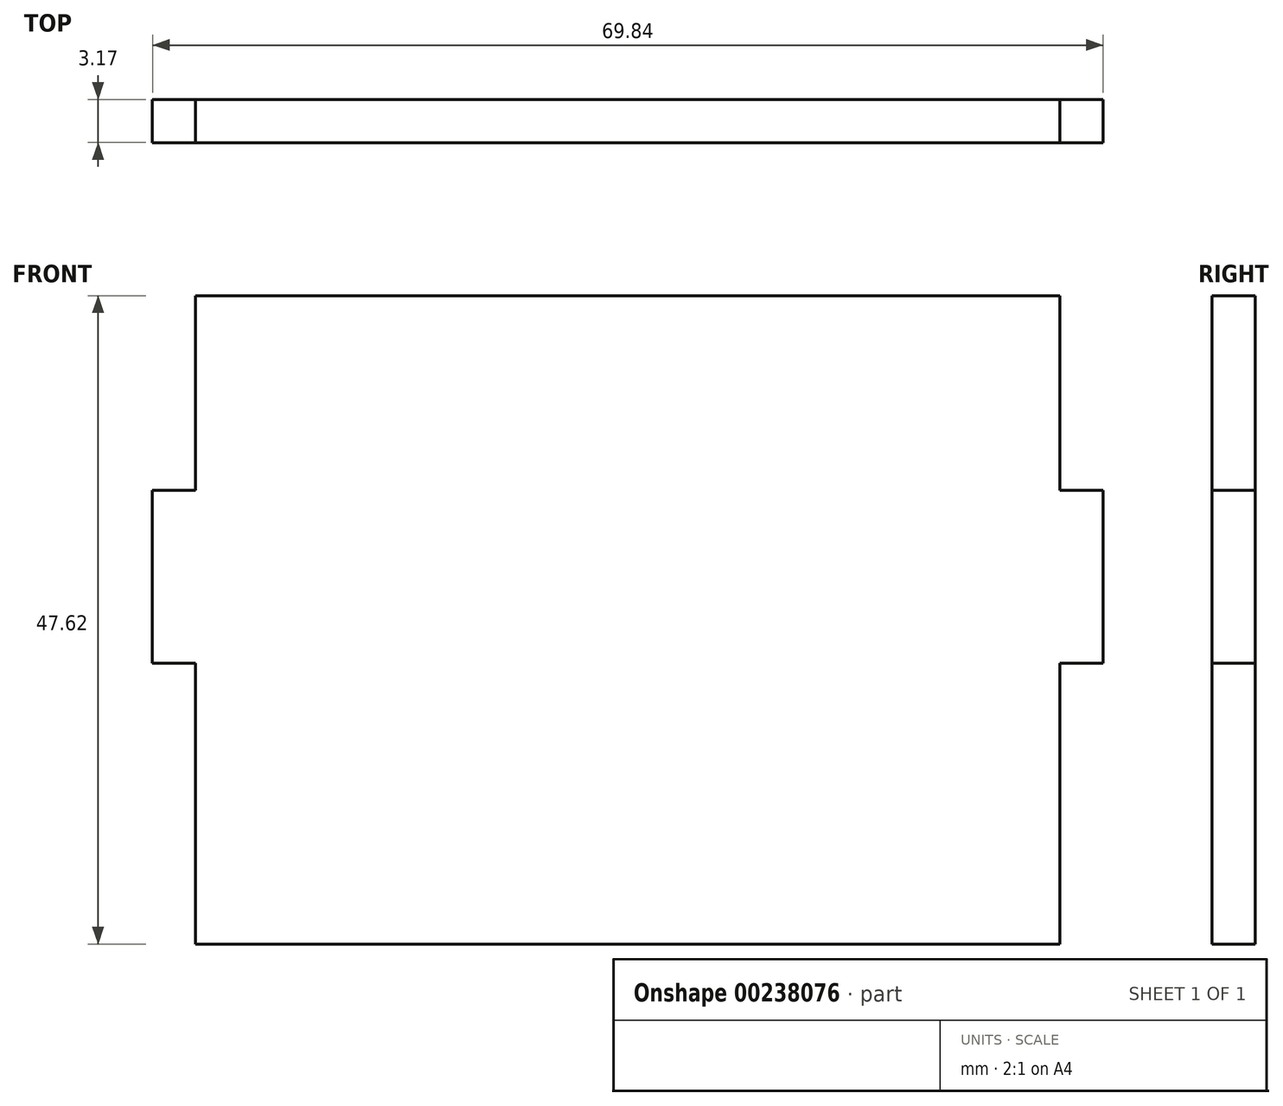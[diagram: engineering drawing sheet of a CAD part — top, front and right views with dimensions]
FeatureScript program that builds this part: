
annotation { "Feature Type Name" : "Feature", "Feature Type Description" : "" }
export const myFeature = defineFeature(function(context is Context, id is Id, definition is map)
    precondition{}
    {
        {
            var Q0;
            Q0=qCreatedBy(makeId("Front.planeOp"),FACE);
            var sketch = newSketch(context, id + "F0", { "sketchPlane" : qUnion([Q0])});
            skLineSegment(sketch, "E0.bottom", {"start": v(31.75, -23.81) * mm, "end": v(-31.75, -23.81) * mm});
            skLineSegment(sketch, "E0.top", {"start": v(31.75, 23.81) * mm, "end": v(-31.75, 23.81) * mm});
            skLineSegment(sketch, "E0.left", {"start": v(31.75, -23.81) * mm, "end": v(31.75, 23.81) * mm});
            skLineSegment(sketch, "E0.right", {"start": v(-31.75, -23.81) * mm, "end": v(-31.75, 23.81) * mm});
            skPoint(sketch, "E0.middle", {"position": v(0, 0) * mm});
            skLineSegment(sketch, "E1.bottom", {"start": v(31.75, 9.52) * mm, "end": v(34.92, 9.52) * mm});
            skLineSegment(sketch, "E1.top", {"start": v(31.75, -3.17) * mm, "end": v(34.92, -3.17) * mm});
            skLineSegment(sketch, "E1.left", {"start": v(31.75, 9.52) * mm, "end": v(31.75, -3.17) * mm});
            skLineSegment(sketch, "E1.right", {"start": v(34.92, 9.52) * mm, "end": v(34.92, -3.17) * mm});
            skLineSegment(sketch, "E2.bottom", {"start": v(-34.92, 9.52) * mm, "end": v(-31.75, 9.52) * mm});
            skLineSegment(sketch, "E2.top", {"start": v(-34.92, -3.17) * mm, "end": v(-31.75, -3.17) * mm});
            skLineSegment(sketch, "E2.left", {"start": v(-34.92, 9.52) * mm, "end": v(-34.92, -3.17) * mm});
            skLineSegment(sketch, "E2.right", {"start": v(-31.75, 9.52) * mm, "end": v(-31.75, -3.17) * mm});
            skLineSegment(sketch, "E3.bottom", {"start": v(-6.35, -23.81) * mm, "end": v(6.35, -23.81) * mm});
            skLineSegment(sketch, "E3.top", {"start": v(-6.35, -26.99) * mm, "end": v(6.35, -26.99) * mm});
            skLineSegment(sketch, "E3.left", {"start": v(-6.35, -23.81) * mm, "end": v(-6.35, -26.99) * mm});
            skLineSegment(sketch, "E3.right", {"start": v(6.35, -23.81) * mm, "end": v(6.35, -26.99) * mm});
            skSolve(sketch);
        }
        {
            var Q0;
            {var subQ4=sQuery(id+"F0.wireOp",EDGE,"E0.top");Q0=makeQuery(id+"F0.imprint","IMPRINT",FACE,{"disambiguationData":[TD([[makeQuery(id+"F0.imprint","IMPRINT",EDGE,{"derivedFrom":subQ4}),1.0]])]});}
            var Q1;
            Q1=makeQuery(id+"F0.imprint","IMPRINT",FACE,{"disambiguationData":[TD([[makeQuery(id+"F0.imprint","IMPRINT",EDGE,{"derivedFrom":sQuery(id+"F0.wireOp",EDGE,"E2.bottom")}),-1.0]])]});
            var Q2;
            Q2=makeQuery(id+"F0.imprint","IMPRINT",FACE,{"disambiguationData":[TD([[makeQuery(id+"F0.imprint","IMPRINT",EDGE,{"derivedFrom":sQuery(id+"F0.wireOp",EDGE,"E3.bottom")}),-1.0]])]});
            var Q3;
            Q3=makeQuery(id+"F0.imprint","IMPRINT",FACE,{"disambiguationData":[TD([[makeQuery(id+"F0.imprint","IMPRINT",EDGE,{"derivedFrom":sQuery(id+"F0.wireOp",EDGE,"E1.bottom")}),-1.0]])]});
            extrude(context, id + "F1", {"entities" : qUnion([Q0, Q1, Q2, Q3]), "depth" : 3.17 * mm});
        }
    });
